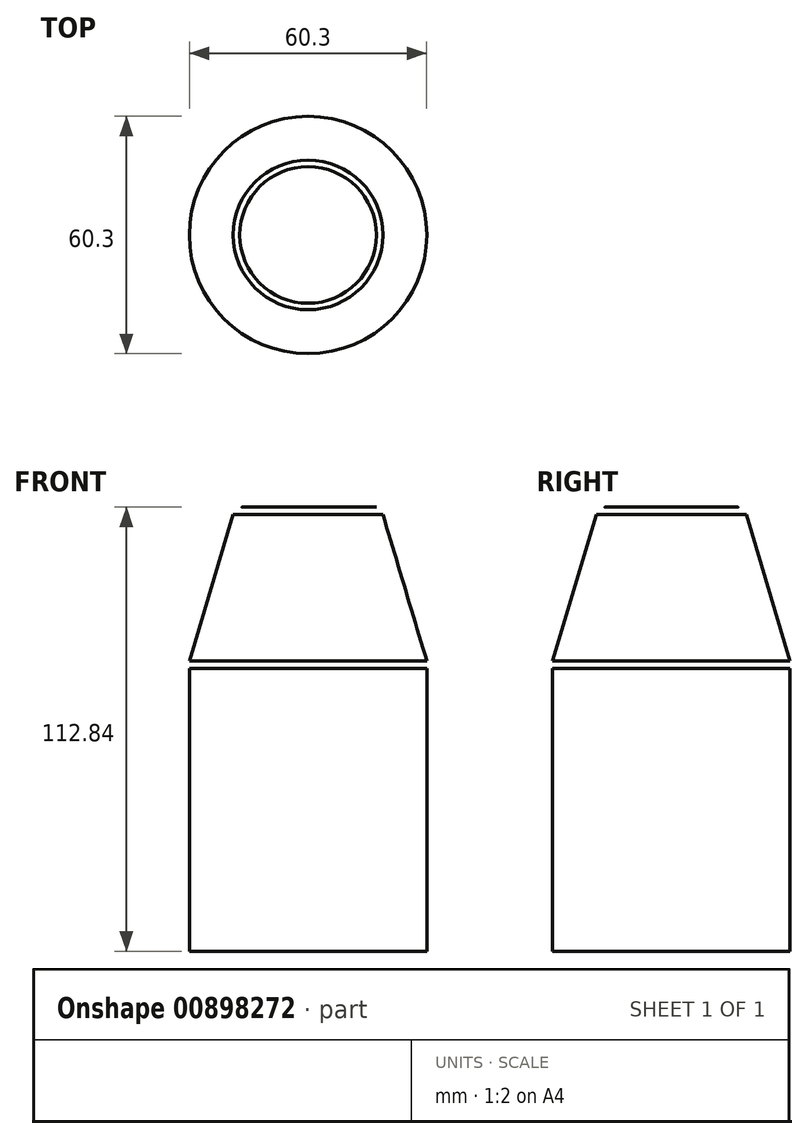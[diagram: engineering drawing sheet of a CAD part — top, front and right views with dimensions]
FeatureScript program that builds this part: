
annotation { "Feature Type Name" : "Feature", "Feature Type Description" : "" }
export const myFeature = defineFeature(function(context is Context, id is Id, definition is map)
    precondition{}
    {
        {
            var Q0;
            Q0=qCreatedBy(makeId("Front.planeOp"),FACE);
            var sketch = newSketch(context, id + "F0", { "sketchPlane" : qUnion([Q0])});
            skLineSegment(sketch, "E0", {"start": v(0, 60.45) * mm, "end": v(17.35, 60.45) * mm});
            skLineSegment(sketch, "E1", {"start": v(17.35, 60.45) * mm, "end": v(19.01, 58.56) * mm});
            skLineSegment(sketch, "E2", {"start": v(19.01, 58.56) * mm, "end": v(30.15, 21.34) * mm});
            skLineSegment(sketch, "E3", {"start": v(30.15, 21.34) * mm, "end": v(30.15, 19.44) * mm});
            skLineSegment(sketch, "E4", {"start": v(30.15, 19.44) * mm, "end": v(30.15, -52.39) * mm});
            skLineSegment(sketch, "E5", {"start": v(30.15, -52.39) * mm, "end": v(0, -52.39) * mm});
            skLineSegment(sketch, "E6", {"start": v(0, -52.39) * mm, "end": v(0, 60.45) * mm});
            skSolve(sketch);
        }
        {
            var Q0;
            Q0 = qSketchRegion(id + "F0", true);
            var Q1;
            Q1=sQuery(id+"F0.wireOp",EDGE,"E0");
            var Q2;
            Q2=sQuery(id+"F0.wireOp",EDGE,"E2");
            var Q3;
            Q3=sQuery(id+"F0.wireOp",EDGE,"E4");
            var Q4;
            Q4=sQuery(id+"F0.wireOp",EDGE,"E6");
            revolve(context, id + "F1", {"bodyType" : ToolBodyType.SURFACE, "surfaceOperationType" : NewSurfaceOperationType.NEW, "entities" : qUnion([Q0]), "surfaceEntities" : qUnion([Q1, Q2, Q3]), "axis" : qUnion([Q4]), "revolveType" : RevolveType.FULL});
        }
    });
